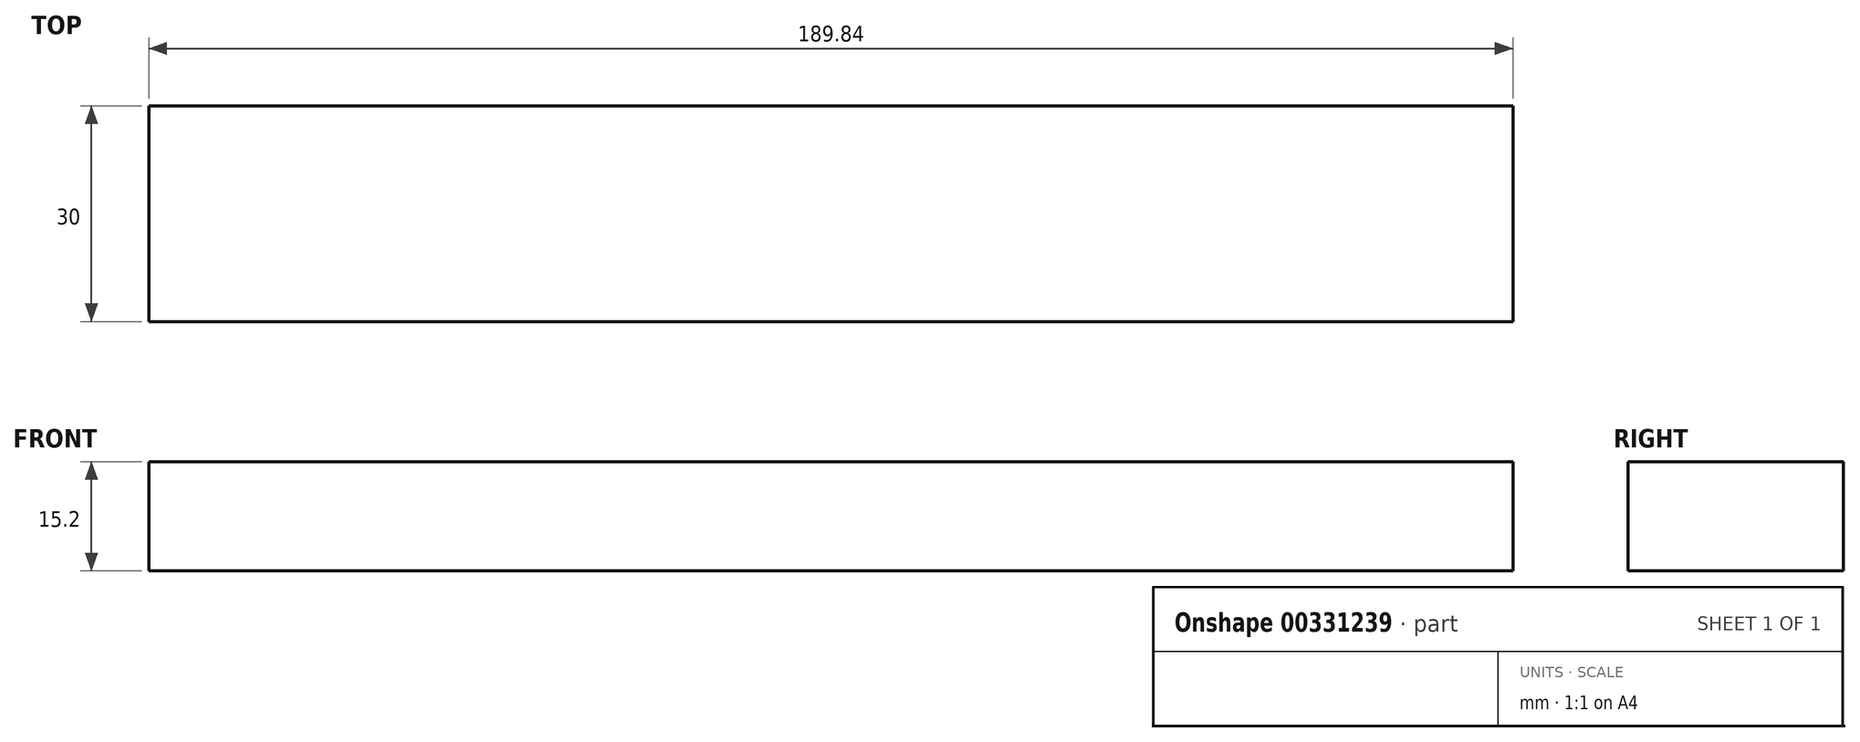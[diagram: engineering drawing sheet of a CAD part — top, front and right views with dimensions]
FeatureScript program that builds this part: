
annotation { "Feature Type Name" : "Feature", "Feature Type Description" : "" }
export const myFeature = defineFeature(function(context is Context, id is Id, definition is map)
    precondition{}
    {
        {
            var Q0;
            Q0=qCreatedBy(makeId("Front.planeOp"),FACE);
            var sketch = newSketch(context, id + "F0", { "sketchPlane" : qUnion([Q0])});
            skLineSegment(sketch, "E0.bottom", {"start": v(-94.92, 7.6) * mm, "end": v(94.92, 7.6) * mm});
            skLineSegment(sketch, "E0.top", {"start": v(-94.92, -7.6) * mm, "end": v(94.92, -7.6) * mm});
            skLineSegment(sketch, "E0.left", {"start": v(-94.92, 7.6) * mm, "end": v(-94.92, -7.6) * mm});
            skLineSegment(sketch, "E0.right", {"start": v(94.92, 7.6) * mm, "end": v(94.92, -7.6) * mm});
            skPoint(sketch, "E0.middle", {"position": v(0, 0) * mm});
            skSolve(sketch);
        }
        {
            var Q0;
            Q0=makeQuery(id+"F0.imprint","IMPRINT",FACE,{"disambiguationData":[TD([[makeQuery(id+"F0.imprint","IMPRINT",EDGE,{"derivedFrom":sQuery(id+"F0.wireOp",EDGE,"E0.bottom")}),-1.0]])]});
            extrude(context, id + "F1", {"entities" : qUnion([Q0]), "endBound" : BoundingType.SYMMETRIC, "depth" : 30 * mm});
        }
    });
